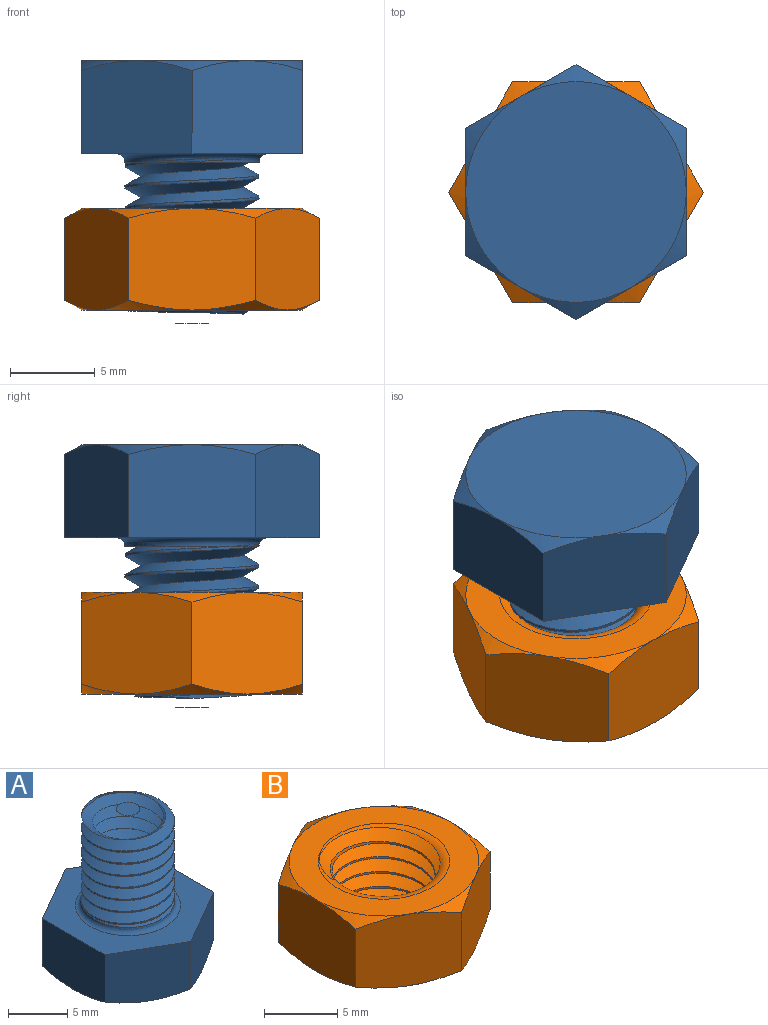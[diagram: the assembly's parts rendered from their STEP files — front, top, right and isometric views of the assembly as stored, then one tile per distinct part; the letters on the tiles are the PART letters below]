
ASSEMBLY  parts=2 mates=1
PART A: 22 faces, bbox 15.6x15.6x16.3 mm
  f0: plane 7.12x6.12mm, normal (0.5,0.87,0), area 39.8mm2, adj f1,f5,f6,f7,f12
  f1: plane 7.12x6.12mm, normal (-0.5,0.87,0), area 39.8mm2, adj f0,f2,f6,f11,f12
  f2: plane 8.13x6.12mm, normal (-1,0,0), area 39.8mm2, adj f1,f3,f6,f10,f11
  f3: plane 7.12x6.12mm, normal (-0.5,-0.87,0), area 39.8mm2, adj f2,f4,f6,f9,f10
  f4: plane 7.12x6.12mm, normal (0.5,-0.87,0), area 39.8mm2, adj f3,f5,f6,f8,f9
  f5: plane 8.13x6.12mm, normal (1,0,0), area 39.8mm2, adj f0,f4,f6,f7,f8
  f6: plane 15.01x13mm, normal (0,0,1), area 84.1mm2, adj f0,f1,f2,f3,f4,f5,f15
  f7: cone r=26.59mm half-angle=60deg, axis (0,0,1), area 4.2mm2, adj f0,f5,f13
  f8: cone r=26.59mm half-angle=60deg, axis (0,0,1), area 4.2mm2, adj f4,f5,f13
  f9: cone r=26.59mm half-angle=60deg, axis (0,0,1), area 4.2mm2, adj f3,f4,f13
  f10: cone r=26.59mm half-angle=60deg, axis (0,0,1), area 4.2mm2, adj f2,f3,f13
  f11: cone r=26.59mm half-angle=60deg, axis (0,0,1), area 4.2mm2, adj f1,f2,f13
  f12: cone r=26.59mm half-angle=60deg, axis (0,0,1), area 4.2mm2, adj f0,f1,f13
  f13: plane 13x13mm, normal (0,0,-1), area 132.7mm2, adj f7,f8,f9,f10,f11,f12
  f14: cylinder r=3.95mm len=8.71mm, axis (0,0,-1), area 42.1mm2, adj f15,f18,f19,f20
  f15: torus R=4.45mm, axis (0,0,1), area 20.4mm2, adj f6,f14,f17
  f16: plane 1.1x0.95mm, normal (0,1,0), area 0.5mm2, adj f17,f18,f19
  f17: cylinder r=3.95mm len=7.9mm, axis (0,0,1), area 22.9mm2, adj f15,f16,f18,f19
  f18: bspline ~10.97x9.12mm, area 196.1mm2, adj f14,f16,f17,f19,f20
  f19: bspline ~10.76x9.12mm, area 184.4mm2, adj f14,f16,f17,f18,f20
  f20: cone r=6.32mm half-angle=75deg, axis (0,0,-1), area 37.6mm2, adj f14,f18,f19,f21
  f21: plane 2x2mm, normal (0,0,1), area 3.1mm2, adj f20
PART B: 26 faces, bbox 15.6x15.6x7.3 mm
  f0: cylinder r=3.5mm len=7mm, axis (0,0,-1), area 10.6mm2, adj f21,f22,f23,f24,f25
  f1: plane 7.12x6.63mm, normal (0.5,0.87,0), area 42mm2, adj f2,f6,f8,f12,f15,f19
  f2: plane 7.12x6.63mm, normal (-0.5,0.87,0), area 42mm2, adj f1,f3,f11,f12,f18,f19
  f3: plane 8.13x6.62mm, normal (-1,0,0), area 42mm2, adj f2,f4,f10,f11,f17,f18
  f4: plane 7.12x6.63mm, normal (-0.5,-0.87,0), area 42mm2, adj f3,f5,f9,f10,f16,f17
  f5: plane 7.12x6.63mm, normal (0.5,-0.87,0), area 42mm2, adj f4,f6,f7,f9,f14,f16
  f6: plane 8.13x6.62mm, normal (1,0,0), area 42mm2, adj f1,f5,f7,f8,f14,f15
  f7: cone r=11.7mm half-angle=60deg, axis (0,0,1), area 4.2mm2, adj f5,f6,f13
  f8: cone r=11.7mm half-angle=60deg, axis (0,0,1), area 4.2mm2, adj f1,f6,f13
  f9: cone r=11.7mm half-angle=60deg, axis (0,0,1), area 4.2mm2, adj f4,f5,f13
  f10: cone r=11.7mm half-angle=60deg, axis (0,0,1), area 4.2mm2, adj f3,f4,f13
  f11: cone r=11.7mm half-angle=60deg, axis (0,0,1), area 4.2mm2, adj f2,f3,f13
  f12: cone r=11.7mm half-angle=60deg, axis (0,0,1), area 4.2mm2, adj f1,f2,f13
  f13: plane 13x13mm, normal (0,0,-1), area 69.1mm2, adj f7,f8,f9,f10,f11,f12,f22
  f14: cone r=11.7mm half-angle=60deg, axis (0,0,-1), area 4.2mm2, adj f5,f6,f20
  f15: cone r=11.7mm half-angle=60deg, axis (0,0,-1), area 4.2mm2, adj f1,f6,f20
  f16: cone r=11.7mm half-angle=60deg, axis (0,0,-1), area 4.2mm2, adj f4,f5,f20
  f17: cone r=11.7mm half-angle=60deg, axis (0,0,-1), area 4.2mm2, adj f3,f4,f20
  f18: cone r=11.7mm half-angle=60deg, axis (0,0,-1), area 4.2mm2, adj f2,f3,f20
  f19: cone r=11.7mm half-angle=60deg, axis (0,0,-1), area 4.2mm2, adj f1,f2,f20
  f20: plane 13x13mm, normal (0,0,1), area 69.1mm2, adj f14,f15,f16,f17,f18,f19,f21
  f21: torus R=4.5mm, axis (0,0,1), area 17.5mm2, adj f0,f20,f24,f25
  f22: torus R=4.5mm, axis (0,0,1), area 30.1mm2, adj f0,f13,f23,f24
  f23: plane 0.95x0.88mm, normal (0,1,0), area 0.4mm2, adj f0,f22,f24,f25
  f24: bspline ~10.28x8.91mm, area 117.1mm2, adj f0,f21,f22,f23,f25
  f25: bspline ~10.28x8.91mm, area 111.4mm2, adj f0,f21,f23,f24
PLACE A rot(axis=(1,0,0),180deg) t=(0,6.5,14.71)mm
PLACE B rot(axis=(-0.71,-0.71,0),180deg) t=(0,6.5,6)mm fixed
MATE cylindrical A.f7 <-> B.f0  axis (0,0,1) through (0,6.5,0)mm
